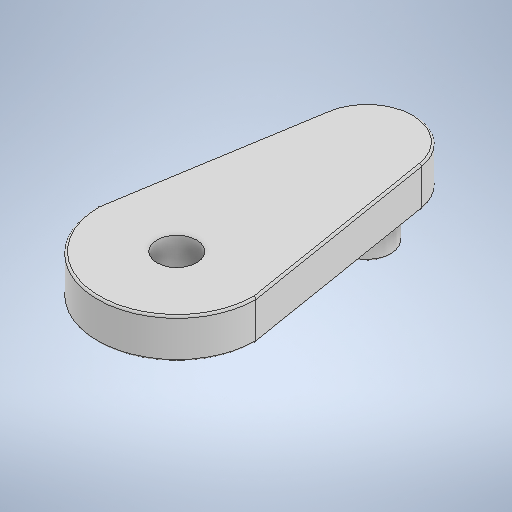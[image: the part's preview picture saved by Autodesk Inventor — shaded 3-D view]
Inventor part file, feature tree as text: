
AUTODESK INVENTOR PART (.ipt)
format: ipt  version: 2025.1 (Build 291241000, 241)  size: 272,896 bytes
history: native  units: mm
features: extrude x3, sketch x3, fillet x1
ambient origin geometry x8: Origin, YZ Plane, XZ Plane, XY Plane, X Axis, Y Axis, Z Axis, Center Point
bodies: Solid1 (feature_tree)
feature tree (7):
  extrude  "Extrusion1"  Depth=24.0mm
  extrude  "Extrusion2"  Depth=10.0mm TaperAngle=0.0deg
  extrude  "Extrusion3"  Depth=0.25mm TaperAngle=0.0deg
  fillet  "Fillet1"  Radius=11.0mm
  sketch  "Sketch1"  dims[d0=24.0mm d1=6.0mm]
  sketch  "Sketch2"  dims[d2=10.0mm d3=5.0mm d4=0.0mm]
  sketch  "Sketch3"  dims[d5=6.0mm d6=11.0mm d7=0.0mm d10=11.0mm d11=0.0mm d12=0.25mm d14=5.0mm]
